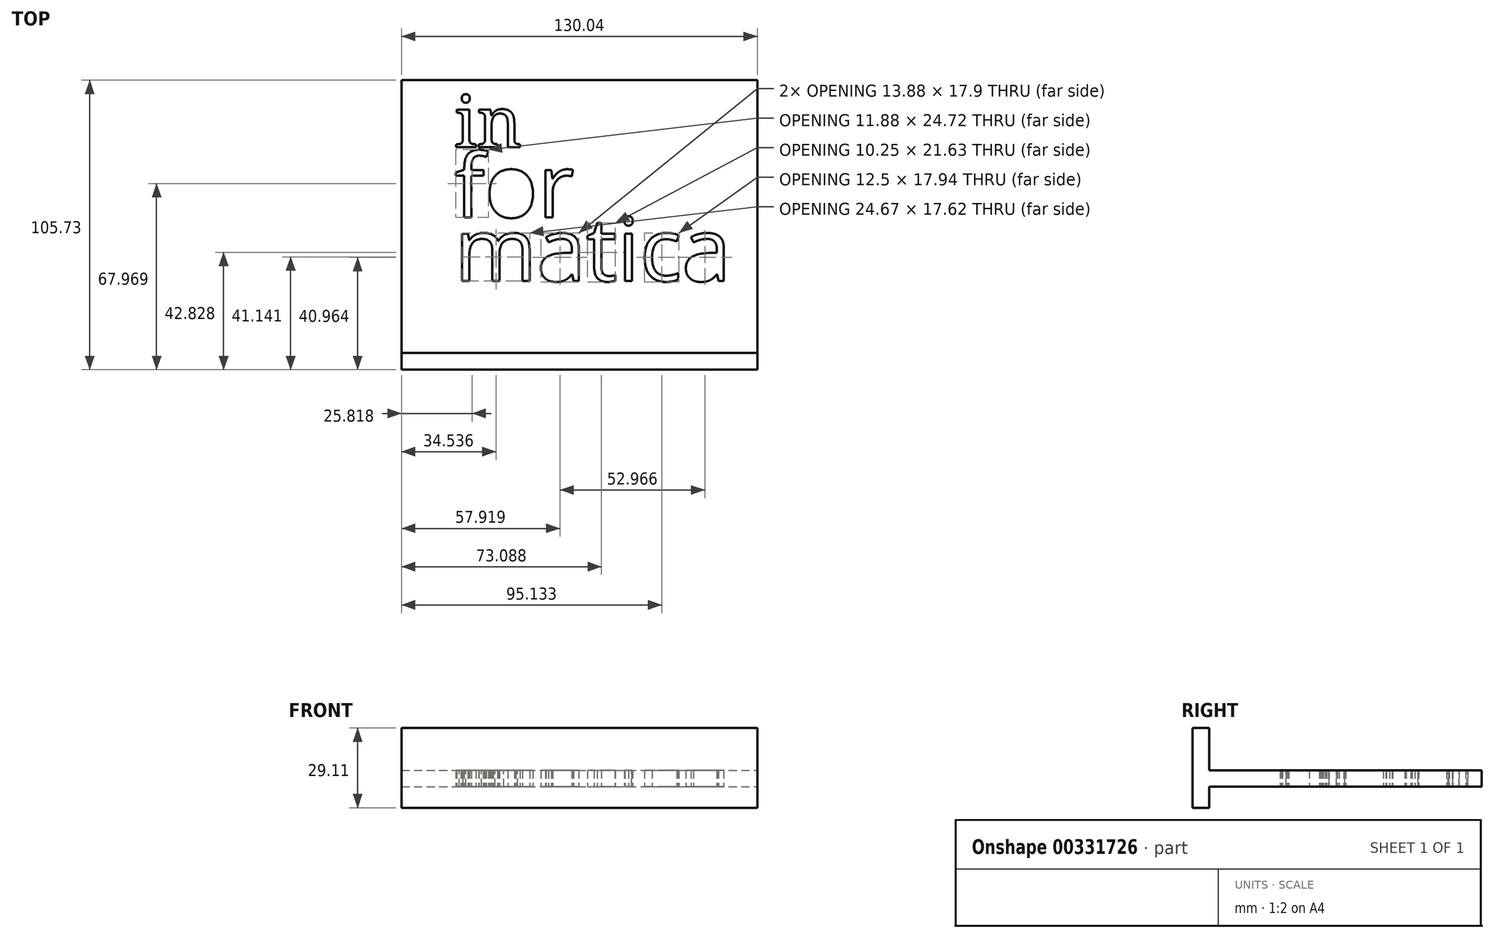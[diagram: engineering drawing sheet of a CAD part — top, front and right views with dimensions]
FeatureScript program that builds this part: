
annotation { "Feature Type Name" : "Feature", "Feature Type Description" : "" }
export const myFeature = defineFeature(function(context is Context, id is Id, definition is map)
    precondition{}
    {
        {
            var Q0;
            Q0=qCreatedBy(makeId("Top.planeOp"),FACE);
            var sketch = newSketch(context, id + "F0", { "sketchPlane" : qUnion([Q0])});
            skLineSegment(sketch, "E0.bottom", {"start": v(65.02, -50.12) * mm, "end": v(-65.02, -50.12) * mm});
            skLineSegment(sketch, "E0.top", {"start": v(65.02, 50.12) * mm, "end": v(-65.02, 50.12) * mm});
            skLineSegment(sketch, "E0.left", {"start": v(65.02, -50.12) * mm, "end": v(65.02, 50.12) * mm});
            skLineSegment(sketch, "E0.right", {"start": v(-65.02, -50.12) * mm, "end": v(-65.02, 50.12) * mm});
            skPoint(sketch, "E0.middle", {"position": v(0, 0) * mm});
            skText(sketch, "E1", { "text": "in", "fontName": "NotoSerif-Regular.ttf"});
            skText(sketch, "E2", { "text": "for", "fontName": "OpenSans-Regular.ttf"});
            skText(sketch, "E3", { "text": "matica", "fontName": "OpenSans-Regular.ttf"});
            const initialGuessF0  = {"E1": [-0.0456, 0.02566, 1, 0, 0.01835], "E2": [-0.0456, 0, 1, 0, 0.02326], "E3": [-0.0456, -0.02328, 1, 0, 0.02328]};
            skSetInitialGuess(sketch, initialGuessF0);
            skSolve(sketch);
        }
        {
            var Q0;
            Q0 = qSketchRegion(id + "F0", true);
            extrude(context, id + "F1", {"entities" : qUnion([Q0]), "depth" : 6 * mm});
        }
        {
            var Q0;
            Q0=qCreatedBy(makeId("Right.planeOp"),FACE);
            var sketch = newSketch(context, id + "F2", { "sketchPlane" : qUnion([Q0])});
            skLineSegment(sketch, "E4.bottom", {"start": v(-55.6, -7.66) * mm, "end": v(-49.5, -7.66) * mm});
            skLineSegment(sketch, "E4.top", {"start": v(-55.6, 21.45) * mm, "end": v(-49.5, 21.45) * mm});
            skLineSegment(sketch, "E4.left", {"start": v(-55.6, -7.66) * mm, "end": v(-55.6, 21.45) * mm});
            skLineSegment(sketch, "E4.right", {"start": v(-49.5, -7.66) * mm, "end": v(-49.5, 21.45) * mm});
            skSolve(sketch);
        }
        {
            var Q0;
            Q0 = qSketchRegion(id + "F2", true);
            var Q1;
            Q1=makeQuery(id+"F1.opExtrude","SWEPT_FACE",FACE,{"disambiguationData":[OSD([sQuery(id+"F0.wireOp",EDGE,"E0.left")])]});
            var Q2;
            Q2=makeQuery(id+"F1.opExtrude","SWEPT_FACE",FACE,{"disambiguationData":[OSD([sQuery(id+"F0.wireOp",EDGE,"E0.right")])]});
            extrude(context, id + "F3", {"entities" : qUnion([Q0]), "operationType" : NewBodyOperationType.ADD, "endBound" : BoundingType.UP_TO_SURFACE, "endBoundEntityFace" : qUnion([Q1]), "depth" : 76.2 * mm, "hasSecondDirection" : true, "secondDirectionBound" : SecondDirectionBoundingType.UP_TO_SURFACE, "secondDirectionOppositeDirection" : true, "secondDirectionBoundEntityFace" : qUnion([Q2]), "secondDirectionDepth" : 76.2 * mm});
        }
    });
